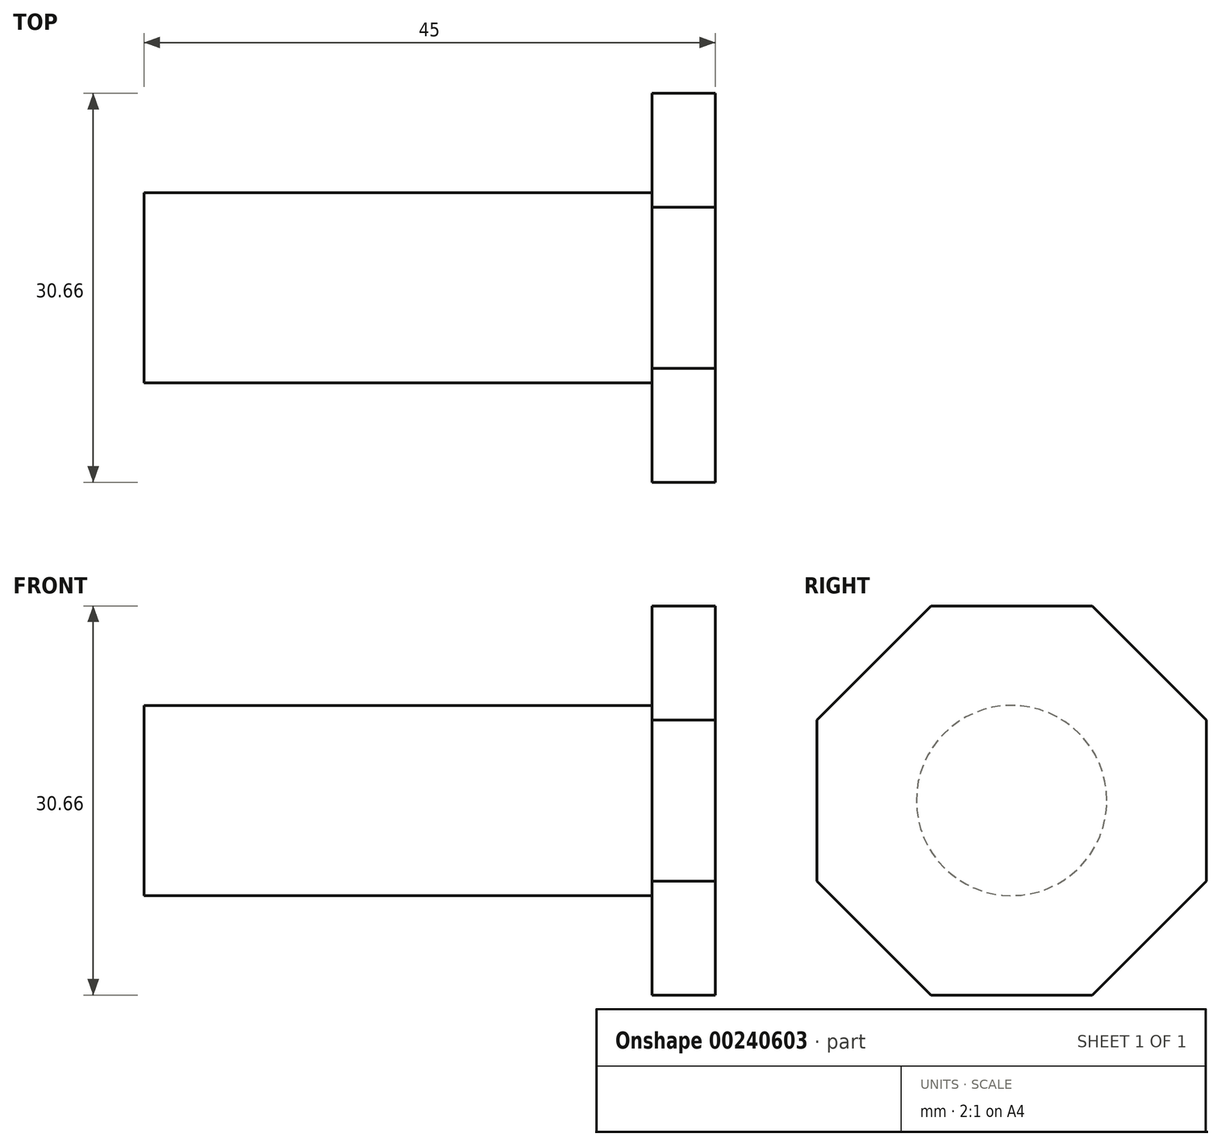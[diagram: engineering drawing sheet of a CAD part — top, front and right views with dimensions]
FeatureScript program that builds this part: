
annotation { "Feature Type Name" : "Feature", "Feature Type Description" : "" }
export const myFeature = defineFeature(function(context is Context, id is Id, definition is map)
    precondition{}
    {
        {
            var Q0;
            Q0=qCreatedBy(makeId("Right.planeOp"),FACE);
            var sketch = newSketch(context, id + "F0", { "sketchPlane" : qUnion([Q0])});
            skCircle(sketch, "E0.cCircle", {"center": v(0, 0) * mm, "radius": 15.33 * mm, "construction": true});
            skLineSegment(sketch, "E0.0", {"start": v(15.33, 6.35) * mm, "end": v(15.33, -6.35) * mm});
            skLineSegment(sketch, "E0.1", {"start": v(15.33, -6.35) * mm, "end": v(6.35, -15.33) * mm});
            skLineSegment(sketch, "E0.2", {"start": v(6.35, -15.33) * mm, "end": v(-6.35, -15.33) * mm});
            skLineSegment(sketch, "E0.3", {"start": v(-6.35, -15.33) * mm, "end": v(-15.33, -6.35) * mm});
            skLineSegment(sketch, "E0.4", {"start": v(-15.33, -6.35) * mm, "end": v(-15.33, 6.35) * mm});
            skLineSegment(sketch, "E0.5", {"start": v(-15.33, 6.35) * mm, "end": v(-6.35, 15.33) * mm});
            skLineSegment(sketch, "E0.6", {"start": v(-6.35, 15.33) * mm, "end": v(6.35, 15.33) * mm});
            skLineSegment(sketch, "E0.7", {"start": v(6.35, 15.33) * mm, "end": v(15.33, 6.35) * mm});
            skPoint(sketch, "E0.0.midPoint", {"position": v(15.33, 0) * mm});
            skSolve(sketch);
        }
        {
            var Q0;
            Q0=qCreatedBy(makeId("Top.planeOp"),FACE);
            var sketch = newSketch(context, id + "F1", { "sketchPlane" : qUnion([Q0])});
            skLineSegment(sketch, "E1.bottom", {"start": v(0, 7.5) * mm, "end": v(-40, 7.5) * mm});
            skLineSegment(sketch, "E1.top", {"start": v(0, -7.5) * mm, "end": v(-40, -7.5) * mm});
            skLineSegment(sketch, "E1.left", {"start": v(0, 7.5) * mm, "end": v(0, -7.5) * mm});
            skLineSegment(sketch, "E1.right", {"start": v(-40, 7.5) * mm, "end": v(-40, -7.5) * mm});
            skPoint(sketch, "E1.middle", {"position": v(-20, 0) * mm});
            skSolve(sketch);
        }
        {
            var Q0;
            Q0 = qSketchRegion(id + "F0", true);
            extrude(context, id + "F2", {"entities" : qUnion([Q0]), "depth" : 5 * mm});
        }
        {
            var Q0;
            Q0 = qSketchRegion(id + "F1", true);
            extrude(context, id + "F3", {"entities" : qUnion([Q0]), "operationType" : NewBodyOperationType.ADD, "endBound" : BoundingType.SYMMETRIC, "depth" : 15 * mm});
        }
        {
            var Q0;
            Q0=makeQuery(id+"F3.opExtrude","CAP_EDGE",EDGE,{"disambiguationData":[OSD([sQuery(id+"F1.wireOp",EDGE,"E1.bottom")])],"isStart":false});
            var Q1;
            Q1=makeQuery(id+"F3.opExtrude","CAP_EDGE",EDGE,{"disambiguationData":[OSD([sQuery(id+"F1.wireOp",EDGE,"E1.bottom")])],"isStart":true});
            var Q2;
            Q2=makeQuery(id+"F3.opExtrude","CAP_EDGE",EDGE,{"disambiguationData":[OSD([sQuery(id+"F1.wireOp",EDGE,"E1.top")])],"isStart":true});
            var Q3;
            Q3=makeQuery(id+"F3.opExtrude","CAP_EDGE",EDGE,{"disambiguationData":[OSD([sQuery(id+"F1.wireOp",EDGE,"E1.top")])],"isStart":false});
            fillet(context, id + "F4", {"entities" : qUnion([Q0, Q1, Q2, Q3]), "radius" : 7.5 * mm, "tangentPropagation" : true, "allowEdgeOverflow" : false});
        }
    });
